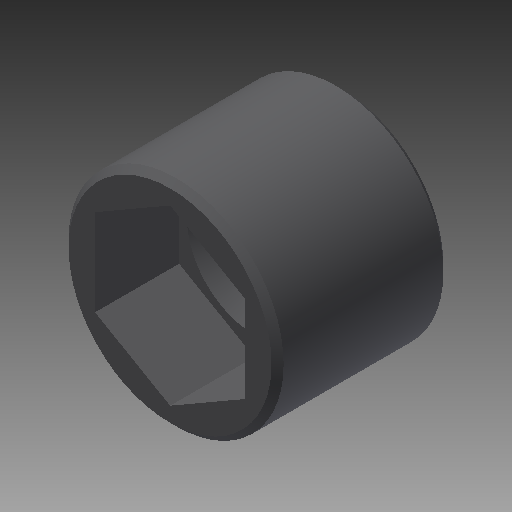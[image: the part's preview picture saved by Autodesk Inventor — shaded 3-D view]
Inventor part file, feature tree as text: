
AUTODESK INVENTOR PART (.ipt)
format: ipt  version: 2017 (Build 210142000, 142)  size: 134,656 bytes
history: native  units: in
note: dims shown in document units (in); Inventor stores cm internally (conversion verified against a paired STEP export)
features: other x7, sketch x2, revolve x1, thread x1, extrude x1
ambient origin geometry x8: Origin, YZ Plane, XZ Plane, XY Plane, X Axis, Y Axis, Z Axis, Center Point
bodies: Solid1 (feature_tree)
feature tree (12):
  revolve  "Revolution1"  [1 undecoded]
  thread  "Thread1"  [1 undecoded]
  extrude  "Extrusion1"  [1 undecoded]
  other  "screw_XY"
  other  "screw_YZ"
  other  "screw_ZX"
  other  "screw_X"
  other  "screw_Y"
  other  "screw_Z"
  other  "screw_Center"
  sketch  "Sketch_1"  dims[d0=360.0deg d1=0.0459in d2=0.0in d3=0.07in d4=0.0in]
  sketch  "Sketch_3"  dims[d5=0.0in]
note: 3 required parameter values undecoded (feature->parameter linkage not recoverable at this tier; creation-order binding heuristic only, values carry confidence <= 0.55)